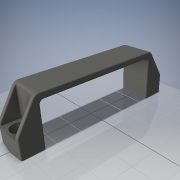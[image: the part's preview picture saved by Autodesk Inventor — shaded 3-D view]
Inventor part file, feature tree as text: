
AUTODESK INVENTOR PART (.ipt)
format: ipt  version: 2016 (Build 200138000, 138)  size: 413,696 bytes
history: native  units: mm
features: fillet x8, extrude x5, sketch x5, mirror x1, projected_geometry x1
ambient origin geometry x8: Origin, YZ Plane, XZ Plane, XY Plane, X Axis, Y Axis, Z Axis, Center Point
bodies: Solid1 (feature_tree)
feature tree (20):
  extrude  "Extrusion1"  Depth=8.5mm
  extrude  "Extrusion2"  Depth=20.0mm
  extrude  "Extrusion3"  Depth=57.5mm
  mirror  "Mirror1"
  extrude  "Extrusion4"  Depth=1.5mm
  sketch  "Sketch6"  dims[d15=26.0mm d16=0.0mm d17=6.0mm d18=5.0mm d19=0.5mm d20=102.0mm d21=0.0mm d22=13.5mm d23=13.5mm d24=5.0mm d25=5.0mm d26=1.0mm d27=3.0mm d28=1.0mm d29=8.5mm d30=0.0mm d31=1.0mm d32=1.0mm d33=3.0mm]
  fillet  "Fillet1"  Radius=40.0mm
  fillet  "Fillet2"  Radius=3.5mm
  fillet  "Fillet3"  Radius=3.5mm
  fillet  "Fillet4"  Radius=16.0mm
  fillet  "Fillet5"  Radius=26.0mm
  extrude  "Extrusion5"  Depth=3.0mm
  fillet  "Fillet6"  Radius=5.0mm
  fillet  "Fillet7"  Radius=0.5mm
  fillet  "Fillet8"  Radius=102.0mm
  sketch  "Sketch1"  dims[d0=26.5mm d1=8.5mm]
  sketch  "Sketch2"  dims[d2=13.25mm d3=20.0mm]
  projected_geometry  "Projected Loop1"
  sketch  "Sketch4"  dims[d4=5.0mm d5=57.5mm]
  sketch  "Sketch5"  dims[d6=17.0mm d7=1.5mm d8=40.0mm d9=0.0mm d10=3.5mm d11=3.5mm d12=16.0mm d13=26.0mm d14=0.0mm]
